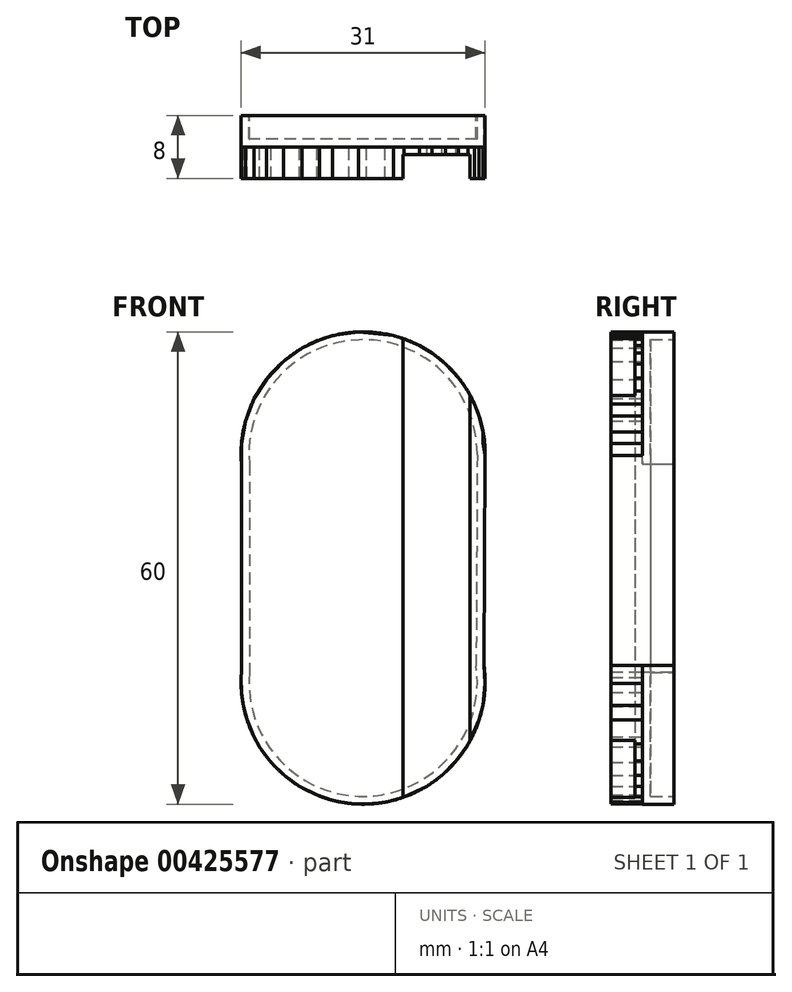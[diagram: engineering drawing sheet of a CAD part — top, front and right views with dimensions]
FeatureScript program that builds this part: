
annotation { "Feature Type Name" : "Feature", "Feature Type Description" : "" }
export const myFeature = defineFeature(function(context is Context, id is Id, definition is map)
    precondition{}
    {
        {
            var Q0;
            Q0=qCreatedBy(makeId("Front.planeOp"),FACE);
            var sketch = newSketch(context, id + "F0", { "sketchPlane" : qUnion([Q0])});
            skArc(sketch, "E0", {"start": v(15.5, 11.5) * mm, "mid": v(-0.56, 27.17) * mm, "end": v(-15.45, 10.38) * mm});
            skArc(sketch, "E1", {"start": v(-15.45, -16.02) * mm, "mid": v(0.4, -32.82) * mm, "end": v(15.36, -15.2) * mm});
            skLineSegment(sketch, "E2", {"start": v(-15.45, 12.98) * mm, "end": v(-15.45, -18.62) * mm});
            skLineSegment(sketch, "E3", {"start": v(15.5, 11.5) * mm, "end": v(15.33, -19.6) * mm});
            skSolve(sketch);
        }
        {
            var Q0;
            Q0 = qSketchRegion(id + "F0", true);
            extrude(context, id + "F1", {"entities" : qUnion([Q0]), "depth" : 4 * mm});
        }
        {
            var Q0;
            Q0=makeQuery(id+"F1.opExtrude","CAP_FACE",FACE,{"disambiguationData":[OSD([sQuery(id+"F0.wireOp",EDGE,"E0"),sQuery(id+"F0.wireOp",EDGE,"E1"),sQuery(id+"F0.wireOp",EDGE,"E2"),sQuery(id+"F0.wireOp",EDGE,"E3")])],"isStart":true});
            shell(context, id + "F2", {"entities" : qUnion([Q0]), "thickness" : 1 * mm});
        }
        {
            var Q0;
            Q0=makeQuery(id+"F1.opExtrude","CAP_FACE",FACE,{"disambiguationData":[OSD([sQuery(id+"F0.wireOp",EDGE,"E0"),sQuery(id+"F0.wireOp",EDGE,"E1"),sQuery(id+"F0.wireOp",EDGE,"E2"),sQuery(id+"F0.wireOp",EDGE,"E3")])],"isStart":false});
            var sketch = newSketch(context, id + "F3", { "sketchPlane" : qUnion([Q0])});
            skLineSegment(sketch, "E4", {"start": v(-15.45, -3.74) * mm, "end": v(-15.45, 10.38) * mm});
            skLineSegment(sketch, "E5", {"start": v(-15.45, 10.38) * mm, "end": v(-15.45, 12.98) * mm});
            skLineSegment(sketch, "E6", {"start": v(-15.45, 12.98) * mm, "end": v(-14.93, 15.83) * mm});
            skLineSegment(sketch, "E7", {"start": v(-14.93, 15.83) * mm, "end": v(-13.83, 18.68) * mm});
            skLineSegment(sketch, "E8", {"start": v(-13.83, 18.68) * mm, "end": v(-12.3, 21.12) * mm});
            skLineSegment(sketch, "E9", {"start": v(-12.3, 21.12) * mm, "end": v(-10.14, 23.4) * mm});
            skLineSegment(sketch, "E10", {"start": v(-10.14, 23.4) * mm, "end": v(-7.75, 25.1) * mm});
            skLineSegment(sketch, "E11", {"start": v(-7.75, 25.1) * mm, "end": v(-5.54, 26.15) * mm});
            skLineSegment(sketch, "E12", {"start": v(-5.54, 26.15) * mm, "end": v(-3.86, 26.69) * mm});
            skLineSegment(sketch, "E13", {"start": v(-3.86, 26.69) * mm, "end": v(-0.56, 27.17) * mm});
            skLineSegment(sketch, "E14", {"start": v(-0.56, 27.17) * mm, "end": v(3.86, 26.69) * mm});
            skLineSegment(sketch, "E15", {"start": v(3.86, 26.69) * mm, "end": v(3.86, 26.69) * mm});
            skLineSegment(sketch, "E16", {"start": v(3.86, 26.69) * mm, "end": v(5.2, 26.28) * mm});
            skLineSegment(sketch, "E17", {"start": v(5.2, 26.28) * mm, "end": v(7.16, 25.43) * mm});
            skLineSegment(sketch, "E18", {"start": v(7.16, 25.43) * mm, "end": v(8.72, 24.49) * mm});
            skLineSegment(sketch, "E19", {"start": v(8.72, 24.49) * mm, "end": v(10.47, 23.11) * mm});
            skLineSegment(sketch, "E20", {"start": v(10.47, 23.11) * mm, "end": v(12.12, 21.34) * mm});
            skLineSegment(sketch, "E21", {"start": v(12.12, 21.34) * mm, "end": v(13.3, 19.65) * mm});
            skLineSegment(sketch, "E22", {"start": v(13.3, 19.65) * mm, "end": v(14.16, 17.99) * mm});
            skLineSegment(sketch, "E23", {"start": v(14.16, 17.99) * mm, "end": v(14.74, 16.46) * mm});
            skLineSegment(sketch, "E24", {"start": v(14.74, 16.46) * mm, "end": v(15.25, 14.45) * mm});
            skLineSegment(sketch, "E25", {"start": v(15.25, 14.45) * mm, "end": v(15.25, 12.98) * mm});
            skLineSegment(sketch, "E26", {"start": v(15.25, 12.98) * mm, "end": v(15.5, 11.5) * mm});
            skLineSegment(sketch, "E27", {"start": v(15.5, 11.5) * mm, "end": v(15.36, -15.2) * mm});
            skLineSegment(sketch, "E28", {"start": v(15.36, -15.2) * mm, "end": v(15.5, -17.5) * mm});
            skLineSegment(sketch, "E29", {"start": v(15.5, -17.5) * mm, "end": v(15.21, -20.3) * mm});
            skLineSegment(sketch, "E30", {"start": v(15.21, -20.3) * mm, "end": v(14.74, -22.1) * mm});
            skLineSegment(sketch, "E31", {"start": v(14.74, -22.1) * mm, "end": v(13.38, -25.15) * mm});
            skLineSegment(sketch, "E32", {"start": v(13.38, -25.15) * mm, "end": v(11.83, -27.34) * mm});
            skLineSegment(sketch, "E33", {"start": v(11.83, -27.34) * mm, "end": v(10, -29.17) * mm});
            skLineSegment(sketch, "E34", {"start": v(10, -29.17) * mm, "end": v(8.1, -30.54) * mm});
            skLineSegment(sketch, "E35", {"start": v(8.1, -30.54) * mm, "end": v(5.2, -31.92) * mm});
            skLineSegment(sketch, "E36", {"start": v(5.2, -31.92) * mm, "end": v(2.76, -32.57) * mm});
            skLineSegment(sketch, "E37", {"start": v(2.76, -32.57) * mm, "end": v(0.4, -32.82) * mm});
            skLineSegment(sketch, "E38", {"start": v(0.4, -32.82) * mm, "end": v(-1.8, -32.72) * mm});
            skLineSegment(sketch, "E39", {"start": v(-1.8, -32.72) * mm, "end": v(-3.86, -32.33) * mm});
            skLineSegment(sketch, "E40", {"start": v(-3.86, -32.33) * mm, "end": v(-5.87, -31.67) * mm});
            skLineSegment(sketch, "E41", {"start": v(-5.87, -31.67) * mm, "end": v(-8.06, -30.56) * mm});
            skLineSegment(sketch, "E42", {"start": v(-8.06, -30.56) * mm, "end": v(-10, -29.16) * mm});
            skLineSegment(sketch, "E43", {"start": v(-10, -29.16) * mm, "end": v(-11.69, -27.5) * mm});
            skLineSegment(sketch, "E44", {"start": v(-11.69, -27.5) * mm, "end": v(-13.15, -25.52) * mm});
            skLineSegment(sketch, "E45", {"start": v(-13.15, -25.52) * mm, "end": v(-13.86, -24.27) * mm});
            skLineSegment(sketch, "E46", {"start": v(-13.86, -24.27) * mm, "end": v(-14.75, -22.08) * mm});
            skLineSegment(sketch, "E47", {"start": v(-14.75, -22.08) * mm, "end": v(-15.2, -20.4) * mm});
            skLineSegment(sketch, "E48", {"start": v(-15.2, -20.4) * mm, "end": v(-15.45, -18.62) * mm});
            skLineSegment(sketch, "E49", {"start": v(-15.45, -18.62) * mm, "end": v(-15.49, -16.73) * mm});
            skLineSegment(sketch, "E50", {"start": v(-15.49, -16.73) * mm, "end": v(-15.45, -16.02) * mm});
            skLineSegment(sketch, "E51", {"start": v(-15.45, -16.02) * mm, "end": v(-15.45, -3.74) * mm});
            skSolve(sketch);
        }
        {
            var Q0;
            Q0 = qSketchRegion(id + "F3", true);
            extrude(context, id + "F4", {"entities" : qUnion([Q0]), "operationType" : NewBodyOperationType.ADD, "depth" : 4 * mm});
        }
        {
            var Q0;
            Q0=makeQuery(id+"F4.opExtrude","CAP_FACE",FACE,{"disambiguationData":[OSD([sQuery(id+"F3.wireOp",EDGE,"E4"),sQuery(id+"F3.wireOp",EDGE,"E5"),sQuery(id+"F3.wireOp",EDGE,"E6"),sQuery(id+"F3.wireOp",EDGE,"E7"),sQuery(id+"F3.wireOp",EDGE,"E8"),sQuery(id+"F3.wireOp",EDGE,"E9"),sQuery(id+"F3.wireOp",EDGE,"E10"),sQuery(id+"F3.wireOp",EDGE,"E11"),sQuery(id+"F3.wireOp",EDGE,"E12"),sQuery(id+"F3.wireOp",EDGE,"E13"),sQuery(id+"F3.wireOp",EDGE,"E14"),sQuery(id+"F3.wireOp",EDGE,"E16"),sQuery(id+"F3.wireOp",EDGE,"E17"),sQuery(id+"F3.wireOp",EDGE,"E18"),sQuery(id+"F3.wireOp",EDGE,"E19"),sQuery(id+"F3.wireOp",EDGE,"E20"),sQuery(id+"F3.wireOp",EDGE,"E21"),sQuery(id+"F3.wireOp",EDGE,"E22"),sQuery(id+"F3.wireOp",EDGE,"E23"),sQuery(id+"F3.wireOp",EDGE,"E24"),sQuery(id+"F3.wireOp",EDGE,"E25"),sQuery(id+"F3.wireOp",EDGE,"E26"),sQuery(id+"F3.wireOp",EDGE,"E27"),sQuery(id+"F3.wireOp",EDGE,"E28"),sQuery(id+"F3.wireOp",EDGE,"E29"),sQuery(id+"F3.wireOp",EDGE,"E30"),sQuery(id+"F3.wireOp",EDGE,"E31"),sQuery(id+"F3.wireOp",EDGE,"E32"),sQuery(id+"F3.wireOp",EDGE,"E33"),sQuery(id+"F3.wireOp",EDGE,"E34"),sQuery(id+"F3.wireOp",EDGE,"E35"),sQuery(id+"F3.wireOp",EDGE,"E36"),sQuery(id+"F3.wireOp",EDGE,"E37"),sQuery(id+"F3.wireOp",EDGE,"E38"),sQuery(id+"F3.wireOp",EDGE,"E39"),sQuery(id+"F3.wireOp",EDGE,"E40"),sQuery(id+"F3.wireOp",EDGE,"E41"),sQuery(id+"F3.wireOp",EDGE,"E42"),sQuery(id+"F3.wireOp",EDGE,"E43"),sQuery(id+"F3.wireOp",EDGE,"E44"),sQuery(id+"F3.wireOp",EDGE,"E45"),sQuery(id+"F3.wireOp",EDGE,"E46"),sQuery(id+"F3.wireOp",EDGE,"E47"),sQuery(id+"F3.wireOp",EDGE,"E48"),sQuery(id+"F3.wireOp",EDGE,"E49"),sQuery(id+"F3.wireOp",EDGE,"E50"),sQuery(id+"F3.wireOp",EDGE,"E51")])],"isStart":false});
            var sketch = newSketch(context, id + "F5", { "sketchPlane" : qUnion([Q0])});
            skPoint(sketch, "E52.oppositeSnap0", {"position": v(13.57, -28.25) * mm});
            skLineSegment(sketch, "E52.bottom", {"start": v(5.07, 27.17) * mm, "end": v(13.57, 27.17) * mm});
            skLineSegment(sketch, "E52.top", {"start": v(5.07, -32.65) * mm, "end": v(13.57, -32.65) * mm});
            skLineSegment(sketch, "E52.left", {"start": v(5.07, 27.17) * mm, "end": v(5.07, -32.65) * mm});
            skLineSegment(sketch, "E52.right", {"start": v(13.57, 27.17) * mm, "end": v(13.57, -32.65) * mm});
            skSolve(sketch);
        }
        {
            var Q0;
            Q0 = qSketchRegion(id + "F5", true);
            extrude(context, id + "F6", {"entities" : qUnion([Q0]), "operationType" : NewBodyOperationType.REMOVE, "oppositeDirection" : true, "depth" : 3 * mm});
        }
    });
